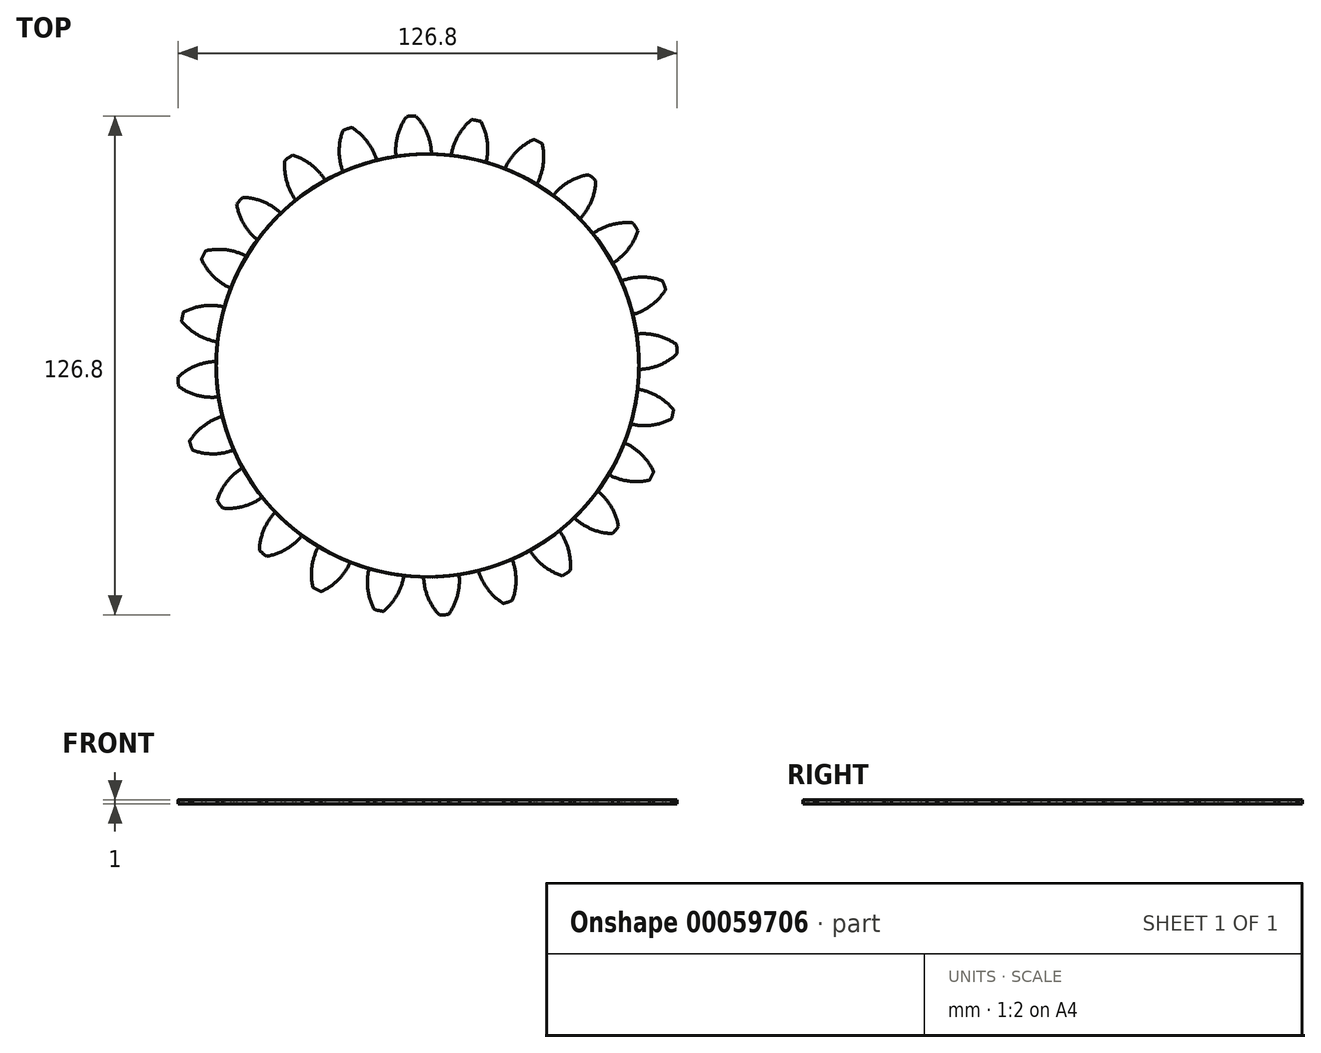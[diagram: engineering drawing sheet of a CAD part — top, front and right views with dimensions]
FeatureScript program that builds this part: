
annotation { "Feature Type Name" : "Feature", "Feature Type Description" : "" }
export const myFeature = defineFeature(function(context is Context, id is Id, definition is map)
    precondition{}
    {
        {
            var Q0;
            Q0=qCreatedBy(makeId("Top.planeOp"),FACE);
            var sketch = newSketch(context, id + "F0", { "sketchPlane" : qUnion([Q0])});
            skCircle(sketch, "E0", {"center": v(0, 0) * mm, "radius": 63.5 * mm, "construction": true});
            skCircle(sketch, "E1", {"center": v(0, 0) * mm, "radius": 58.67 * mm, "construction": true});
            skCircle(sketch, "E2", {"center": v(0, 0) * mm, "radius": 53.72 * mm});
            skLineSegment(sketch, "E3", {"start": v(0, 0) * mm, "end": v(0, 79.09) * mm, "construction": true});
            skLineSegment(sketch, "E4", {"start": v(0, 0) * mm, "end": v(-5.21, 79.56) * mm, "construction": true});
            skLineSegment(sketch, "E5", {"start": v(0, 58.67) * mm, "end": v(-71.52, 58.67) * mm, "construction": true});
            skLineSegment(sketch, "E6", {"start": v(0, 58.67) * mm, "end": v(-70.22, 33.12) * mm, "construction": true});
            skCircle(sketch, "E7", {"center": v(0, 58.67) * mm, "radius": 14.6 * mm, "construction": true});
            skCircle(sketch, "E8", {"center": v(0, 0) * mm, "radius": 55.14 * mm, "construction": true});
            skCircle(sketch, "E9", {"center": v(-13.61, 53.4) * mm, "radius": 14.6 * mm, "construction": true});
            skArc(sketch, "E10", {"start": v(1, 53.69) * mm, "mid": v(0.72, 56.22) * mm, "end": v(0, 58.67) * mm});
            skArc(sketch, "E11", {"start": v(0, 58.67) * mm, "mid": v(-1.26, 61.18) * mm, "end": v(-2.98, 63.4) * mm});
            skArc(sketch, "E12.MirrorCS", {"start": v(-7.66, 58.17) * mm, "mid": v(-6.74, 60.82) * mm, "end": v(-5.32, 63.25) * mm});
            skArc(sketch, "E13.MirrorCS", {"start": v(-8, 53.1) * mm, "mid": v(-8.05, 55.65) * mm, "end": v(-7.66, 58.17) * mm});
            skArc(sketch, "E14", {"start": v(-2.98, 63.4) * mm, "mid": v(-4.15, 63.36) * mm, "end": v(-5.32, 63.25) * mm});
            skSolve(sketch);
        }
        {
            var Q0;
            Q0 = qSketchRegion(id + "F0", true);
            extrude(context, id + "F1", {"entities" : qUnion([Q0]), "depth" : 1 * mm});
        }
        {
            var Q0;
            Q0=makeQuery(id+"F1.opExtrude","SWEPT_BODY",BODY,{"disambiguationData":[OSD([sQuery(id+"F0.wireOp",EDGE,"E2"),sQuery(id+"F0.wireOp",EDGE,"E10"),sQuery(id+"F0.wireOp",EDGE,"E11"),sQuery(id+"F0.wireOp",EDGE,"E12.MirrorCS"),sQuery(id+"F0.wireOp",EDGE,"E13.MirrorCS"),sQuery(id+"F0.wireOp",EDGE,"E14")])]});
            var Q1;
            Q1=makeQuery(id+"F1.opExtrude","SWEPT_FACE",FACE,{"disambiguationData":[OSD([sQuery(id+"F0.wireOp",EDGE,"E2")])]});
            circularPattern(context, id + "F2", {"entities" : qUnion([Q0]), "axis" : qUnion([Q1]), "angle" : 15 * degree, "instanceCount" : 24});
        }
    });
